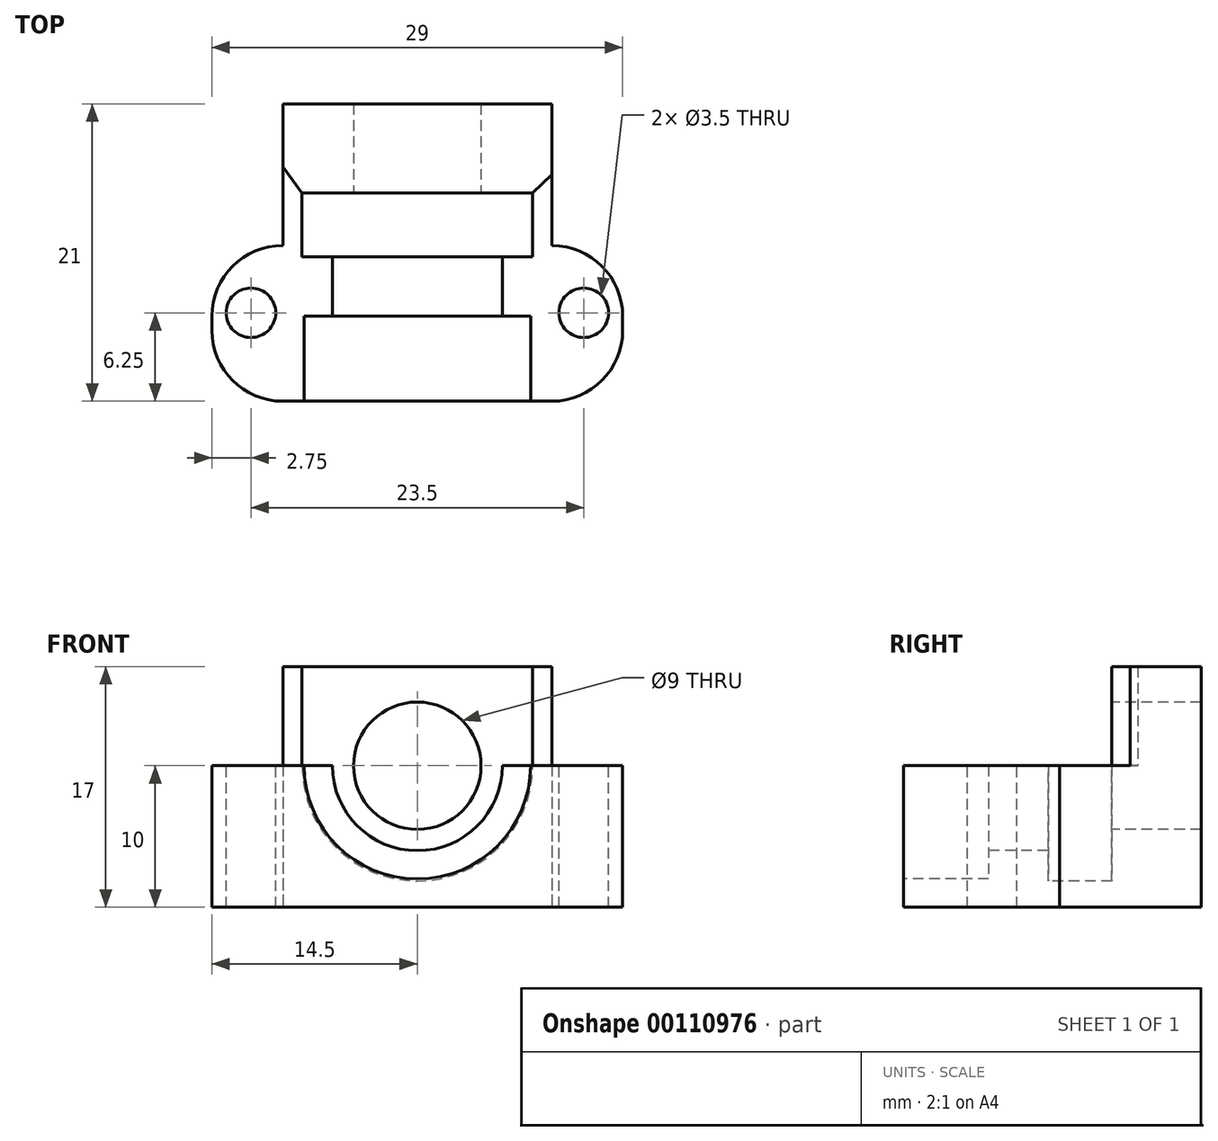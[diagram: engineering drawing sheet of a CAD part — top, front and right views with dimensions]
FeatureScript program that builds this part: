
annotation { "Feature Type Name" : "Feature", "Feature Type Description" : "" }
export const myFeature = defineFeature(function(context is Context, id is Id, definition is map)
    precondition{}
    {
        {
            var Q0;
            Q0=qCreatedBy(makeId("Top.planeOp"),FACE);
            var sketch = newSketch(context, id + "F0", { "sketchPlane" : qUnion([Q0])});
            skLineSegment(sketch, "E0.bottom", {"start": v(0, 0) * mm, "end": v(25, 0) * mm});
            skLineSegment(sketch, "E0.top", {"start": v(0, 11) * mm, "end": v(25, 11) * mm});
            skLineSegment(sketch, "E0.left", {"start": v(0, 0) * mm, "end": v(0, 11) * mm});
            skLineSegment(sketch, "E0.right", {"start": v(25, 0) * mm, "end": v(25, 11) * mm});
            skSolve(sketch);
        }
        {
            var Q0;
            Q0=qSketchRegion(id+"F0",true);
            extrude(context, id + "F1", {"entities" : qUnion([Q0]), "depth" : 10 * mm});
        }
        {
            var Q0;
            Q0=makeQuery(id+"F1.opExtrude","SWEPT_FACE",FACE,{"disambiguationData":[OSD([sQuery(id+"F0.wireOp",EDGE,"E0.bottom")])]});
            var sketch = newSketch(context, id + "F2", { "sketchPlane" : qUnion([Q0])});
            skCircle(sketch, "E1", {"center": v(12.5, 10) * mm, "radius": 8 * mm});
            skSolve(sketch);
        }
        {
            var Q0;
            Q0=qSketchRegion(id+"F2",true);
            extrude(context, id + "F3", {"entities" : qUnion([Q0]), "operationType" : NewBodyOperationType.REMOVE, "oppositeDirection" : true, "depth" : 6 * mm});
        }
        {
            var Q0;
            Q0=makeQuery(id+"F3.boolean.opBoolean","COPY",FACE,{"derivedFrom":makeQuery(id+"F3.opExtrude","CAP_FACE",FACE,{"disambiguationData":[OSD([sQuery(id+"F2.wireOp",EDGE,"E1")])],"isStart":false})});
            var sketch = newSketch(context, id + "F4", { "sketchPlane" : qUnion([Q0])});
            skCircle(sketch, "E2", {"center": v(12.5, 10) * mm, "radius": 6 * mm});
            skSolve(sketch);
        }
        {
            var Q0;
            Q0=qSketchRegion(id+"F4",true);
            extrude(context, id + "F5", {"entities" : qUnion([Q0]), "operationType" : NewBodyOperationType.REMOVE, "oppositeDirection" : true, "depth" : 4.2 * mm});
        }
        {
            var Q0;
            Q0=makeQuery(id+"F1.opExtrude","SWEPT_FACE",FACE,{"disambiguationData":[OSD([sQuery(id+"F0.wireOp",EDGE,"E0.left")])]});
            var sketch = newSketch(context, id + "F6", { "sketchPlane" : qUnion([Q0])});
            skLineSegment(sketch, "E3.bottom", {"start": v(-11, 0) * mm, "end": v(0, 0) * mm});
            skLineSegment(sketch, "E3.top", {"start": v(-11, 10) * mm, "end": v(0, 10) * mm});
            skLineSegment(sketch, "E3.left", {"start": v(-11, 0) * mm, "end": v(-11, 10) * mm});
            skLineSegment(sketch, "E3.right", {"start": v(0, 0) * mm, "end": v(0, 10) * mm});
            skSolve(sketch);
        }
        {
            var Q0;
            Q0=qSketchRegion(id+"F6",true);
            extrude(context, id + "F7", {"entities" : qUnion([Q0]), "operationType" : NewBodyOperationType.ADD, "depth" : 2 * mm});
        }
        {
            var Q0;
            Q0=makeQuery(id+"F1.opExtrude","SWEPT_FACE",FACE,{"disambiguationData":[OSD([sQuery(id+"F0.wireOp",EDGE,"E0.right")])]});
            var sketch = newSketch(context, id + "F8", { "sketchPlane" : qUnion([Q0])});
            skLineSegment(sketch, "E4.bottom", {"start": v(11, 10) * mm, "end": v(0, 10) * mm});
            skLineSegment(sketch, "E4.top", {"start": v(11, 0) * mm, "end": v(0, 0) * mm});
            skLineSegment(sketch, "E4.left", {"start": v(11, 10) * mm, "end": v(11, 0) * mm});
            skLineSegment(sketch, "E4.right", {"start": v(0, 10) * mm, "end": v(0, 0) * mm});
            skSolve(sketch);
        }
        {
            var Q0;
            Q0=qSketchRegion(id+"F8",true);
            extrude(context, id + "F9", {"entities" : qUnion([Q0]), "operationType" : NewBodyOperationType.ADD, "depth" : 2 * mm});
        }
        {
            var Q0;
            Q0=makeQuery(id+"F9.opExtrude","CAP_EDGE",EDGE,{"disambiguationData":[OSD([sQuery(id+"F8.wireOp",EDGE,"E4.left")])],"isStart":false});
            var Q1;
            Q1=makeQuery(id+"F9.opExtrude","CAP_EDGE",EDGE,{"disambiguationData":[OSD([sQuery(id+"F8.wireOp",EDGE,"E4.right")])],"isStart":false});
            var Q2;
            Q2=makeQuery(id+"F7.opExtrude","CAP_EDGE",EDGE,{"disambiguationData":[OSD([sQuery(id+"F6.wireOp",EDGE,"E3.left")])],"isStart":false});
            var Q3;
            Q3=makeQuery(id+"F7.opExtrude","CAP_EDGE",EDGE,{"disambiguationData":[OSD([sQuery(id+"F6.wireOp",EDGE,"E3.right")])],"isStart":false});
            fillet(context, id + "F10", {"entities" : qUnion([Q0, Q1, Q2, Q3]), "radius" : 5 * mm, "tangentPropagation" : true, "allowEdgeOverflow" : false});
        }
        {
            var Q0;
            {var subQ0=sQuery(id+"F0.wireOp",EDGE,"E0.bottom");var subQ1=sQuery(id+"F0.wireOp",EDGE,"E0.top");var subQ2=sQuery(id+"F0.wireOp",EDGE,"E0.left");Q0=makeQuery(id+"F5.boolean.opBoolean","SPLIT",FACE,{"disambiguationData":[TD([makeQuery(id+"F1.opExtrude","SWEPT_FACE",FACE,{"disambiguationData":[OSD([subQ2])]})])],"derivedFrom":makeQuery(id+"F1.opExtrude","CAP_FACE",FACE,{"disambiguationData":[OSD([subQ0,subQ1,subQ2,sQuery(id+"F0.wireOp",EDGE,"E0.right")])],"isStart":false})});}
            var sketch = newSketch(context, id + "F11", { "sketchPlane" : qUnion([Q0])});
            skCircle(sketch, "E5", {"center": v(0.75, 6.25) * mm, "radius": 1.75 * mm});
            skCircle(sketch, "E6", {"center": v(24.25, 6.25) * mm, "radius": 1.75 * mm});
            skSolve(sketch);
        }
        {
            var Q0;
            Q0=qSketchRegion(id+"F11",true);
            extrude(context, id + "F12", {"entities" : qUnion([Q0]), "operationType" : NewBodyOperationType.REMOVE, "oppositeDirection" : true, "depth" : 25 * mm});
        }
        {
            var Q0;
            Q0=makeQuery(id+"F9.boolean.opBoolean","MERGE",FACE,{"derivedFrom":[makeQuery(id+"F7.boolean.opBoolean","MERGE",FACE,{"derivedFrom":[makeQuery(id+"F1.opExtrude","SWEPT_FACE",FACE,{"disambiguationData":[OSD([sQuery(id+"F0.wireOp",EDGE,"E0.top")])]}),makeQuery(id+"F7.opExtrude","SWEPT_FACE",FACE,{"disambiguationData":[OSD([sQuery(id+"F6.wireOp",EDGE,"E3.left")])]})]}),makeQuery(id+"F9.opExtrude","SWEPT_FACE",FACE,{"disambiguationData":[OSD([sQuery(id+"F8.wireOp",EDGE,"E4.left")])]})]});
            extrude(context, id + "F13", {"entities" : qUnion([Q0]), "operationType" : NewBodyOperationType.ADD, "depth" : 10 * mm});
        }
        {
            var Q0;
            Q0=makeQuery(id+"F5.boolean.opBoolean","COPY",FACE,{"derivedFrom":makeQuery(id+"F5.opExtrude","CAP_FACE",FACE,{"disambiguationData":[OSD([sQuery(id+"F4.wireOp",EDGE,"E2")])],"isStart":false})});
            var sketch = newSketch(context, id + "F14", { "sketchPlane" : qUnion([Q0])});
            skCircle(sketch, "E7", {"center": v(12.5, 10) * mm, "radius": 8.14 * mm});
            skSolve(sketch);
        }
        {
            var Q0;
            Q0=qSketchRegion(id+"F14",true);
            extrude(context, id + "F15", {"entities" : qUnion([Q0]), "operationType" : NewBodyOperationType.REMOVE, "oppositeDirection" : true, "depth" : 4.5 * mm});
        }
        {
            var Q0;
            {var subQ0=sQuery(id+"F8.wireOp",EDGE,"E4.bottom");var subQ1=sQuery(id+"F6.wireOp",EDGE,"E3.top");var subQ2=sQuery(id+"F0.wireOp",EDGE,"E0.top");Q0=makeQuery(id+"F13.boolean.opBoolean","MERGE",FACE,{"derivedFrom":[makeQuery(id+"F9.boolean.opBoolean","MERGE",FACE,{"derivedFrom":[makeQuery(id+"F7.boolean.opBoolean","MERGE",FACE,{"derivedFrom":[makeQuery(id+"F1.opExtrude","CAP_FACE",FACE,{"disambiguationData":[OSD([sQuery(id+"F0.wireOp",EDGE,"E0.bottom"),subQ2,sQuery(id+"F0.wireOp",EDGE,"E0.left"),sQuery(id+"F0.wireOp",EDGE,"E0.right")])],"isStart":false}),makeQuery(id+"F7.opExtrude","SWEPT_FACE",FACE,{"disambiguationData":[OSD([subQ1])]})]}),makeQuery(id+"F9.opExtrude","SWEPT_FACE",FACE,{"disambiguationData":[OSD([subQ0])]})]}),makeQuery(id+"F13.opExtrude","SWEPT_FACE",FACE,{"disambiguationData":[OSD([subQ2,subQ1,sQuery(id+"F6.wireOp",EDGE,"E3.left"),subQ0,sQuery(id+"F8.wireOp",EDGE,"E4.left")])]})]});}
            var sketch = newSketch(context, id + "F16", { "sketchPlane" : qUnion([Q0])});
            skLineSegment(sketch, "E8", {"start": v(4.36, 14.7) * mm, "end": v(3, 16.54) * mm});
            skLineSegment(sketch, "E9", {"start": v(3, 16.54) * mm, "end": v(3, 21) * mm});
            skLineSegment(sketch, "E10", {"start": v(3, 21) * mm, "end": v(22, 21) * mm});
            skLineSegment(sketch, "E11", {"start": v(22, 21) * mm, "end": v(22, 16) * mm});
            skLineSegment(sketch, "E12", {"start": v(22, 16) * mm, "end": v(20.64, 14.7) * mm});
            skLineSegment(sketch, "E13", {"start": v(20.64, 14.7) * mm, "end": v(4.36, 14.7) * mm});
            skSolve(sketch);
        }
        {
            var Q0;
            Q0=makeQuery(id+"F16.imprint","IMPRINT",FACE,{"disambiguationData":[TD([[makeQuery(id+"F16.imprint","IMPRINT",EDGE,{"derivedFrom":sQuery(id+"F16.wireOp",EDGE,"E8")}),-1.0]])]});
            extrude(context, id + "F17", {"entities" : qUnion([Q0]), "operationType" : NewBodyOperationType.ADD, "depth" : 7 * mm});
        }
        {
            var Q0;
            Q0=makeQuery(id+"F17.boolean.opBoolean","MERGE",FACE,{"derivedFrom":[makeQuery(id+"F15.boolean.opBoolean","COPY",FACE,{"derivedFrom":makeQuery(id+"F15.opExtrude","CAP_FACE",FACE,{"disambiguationData":[OSD([sQuery(id+"F14.wireOp",EDGE,"E7")])],"isStart":false})}),makeQuery(id+"F17.opExtrude","SWEPT_FACE",FACE,{"disambiguationData":[OSD([sQuery(id+"F16.wireOp",EDGE,"E13")])]})]});
            var sketch = newSketch(context, id + "F18", { "sketchPlane" : qUnion([Q0])});
            skCircle(sketch, "E14", {"center": v(12.5, 10) * mm, "radius": 4.5 * mm});
            skSolve(sketch);
        }
        {
            var Q0;
            Q0=qSketchRegion(id+"F18",true);
            extrude(context, id + "F19", {"entities" : qUnion([Q0]), "operationType" : NewBodyOperationType.REMOVE, "oppositeDirection" : true, "depth" : 25 * mm});
        }
    });
